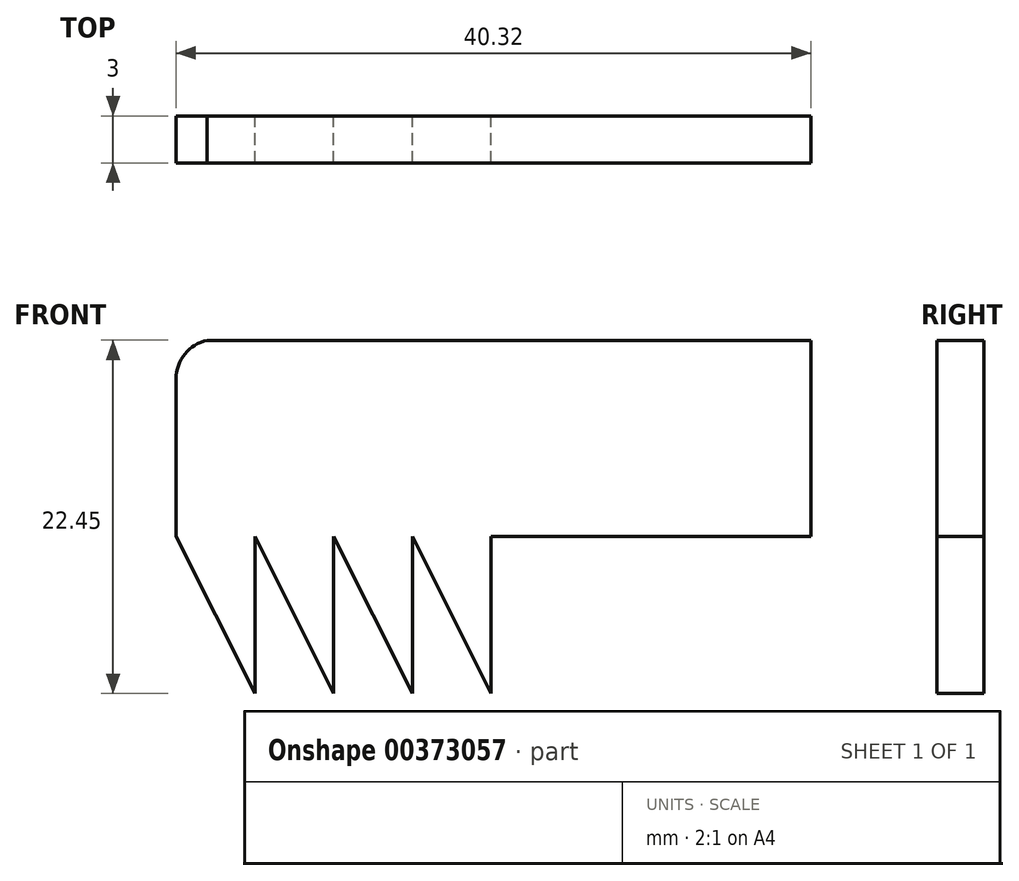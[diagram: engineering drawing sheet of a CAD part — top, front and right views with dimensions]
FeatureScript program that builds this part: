
annotation { "Feature Type Name" : "Feature", "Feature Type Description" : "" }
export const myFeature = defineFeature(function(context is Context, id is Id, definition is map)
    precondition{}
    {
        {
            var Q0;
            Q0=qCreatedBy(makeId("Front.planeOp"),FACE);
            var sketch = newSketch(context, id + "F0", { "sketchPlane" : qUnion([Q0])});
            skLineSegment(sketch, "E0.right", {"start": v(20, 0) * mm, "end": v(20, 10) * mm});
            skLineSegment(sketch, "E1", {"start": v(20, 0) * mm, "end": v(15, 10) * mm});
            skLineSegment(sketch, "E2", {"start": v(10, 10) * mm, "end": v(15, 0) * mm});
            skLineSegment(sketch, "E3", {"start": v(10, 0) * mm, "end": v(5, 10) * mm});
            skLineSegment(sketch, "E4", {"start": v(0, 10) * mm, "end": v(5, 0) * mm});
            skPoint(sketch, "E5.orphan", {"position": v(0, 0) * mm});
            skLineSegment(sketch, "E6", {"start": v(5, 10) * mm, "end": v(5, 0) * mm});
            skLineSegment(sketch, "E7", {"start": v(10, 10) * mm, "end": v(10, 0) * mm});
            skLineSegment(sketch, "E8", {"start": v(15, 10) * mm, "end": v(15, 0) * mm});
            skLineSegment(sketch, "E9", {"start": v(0, 10) * mm, "end": v(0, 20) * mm});
            skArc(sketch, "E10", {"start": v(1.98, 22.45) * mm, "mid": v(0.56, 21.57) * mm, "end": v(0, 20) * mm});
            skLineSegment(sketch, "E11", {"start": v(1.98, 22.45) * mm, "end": v(20, 22.45) * mm});
            skLineSegment(sketch, "E12", {"start": v(20, 22.45) * mm, "end": v(40.32, 22.45) * mm});
            skLineSegment(sketch, "E13", {"start": v(40.32, 22.45) * mm, "end": v(40.32, 10) * mm});
            skLineSegment(sketch, "E14", {"start": v(40.32, 10) * mm, "end": v(20, 10) * mm});
            skSolve(sketch);
        }
        {
            var Q0;
            Q0=makeQuery(id+"F0.imprint","IMPRINT",FACE,{"disambiguationData":[TD([[makeQuery(id+"F0.imprint","IMPRINT",EDGE,{"derivedFrom":sQuery(id+"F0.wireOp",EDGE,"E0.right")}),1.0]])]});
            extrude(context, id + "F1", {"entities" : qUnion([Q0]), "depth" : 3 * mm});
        }
    });
